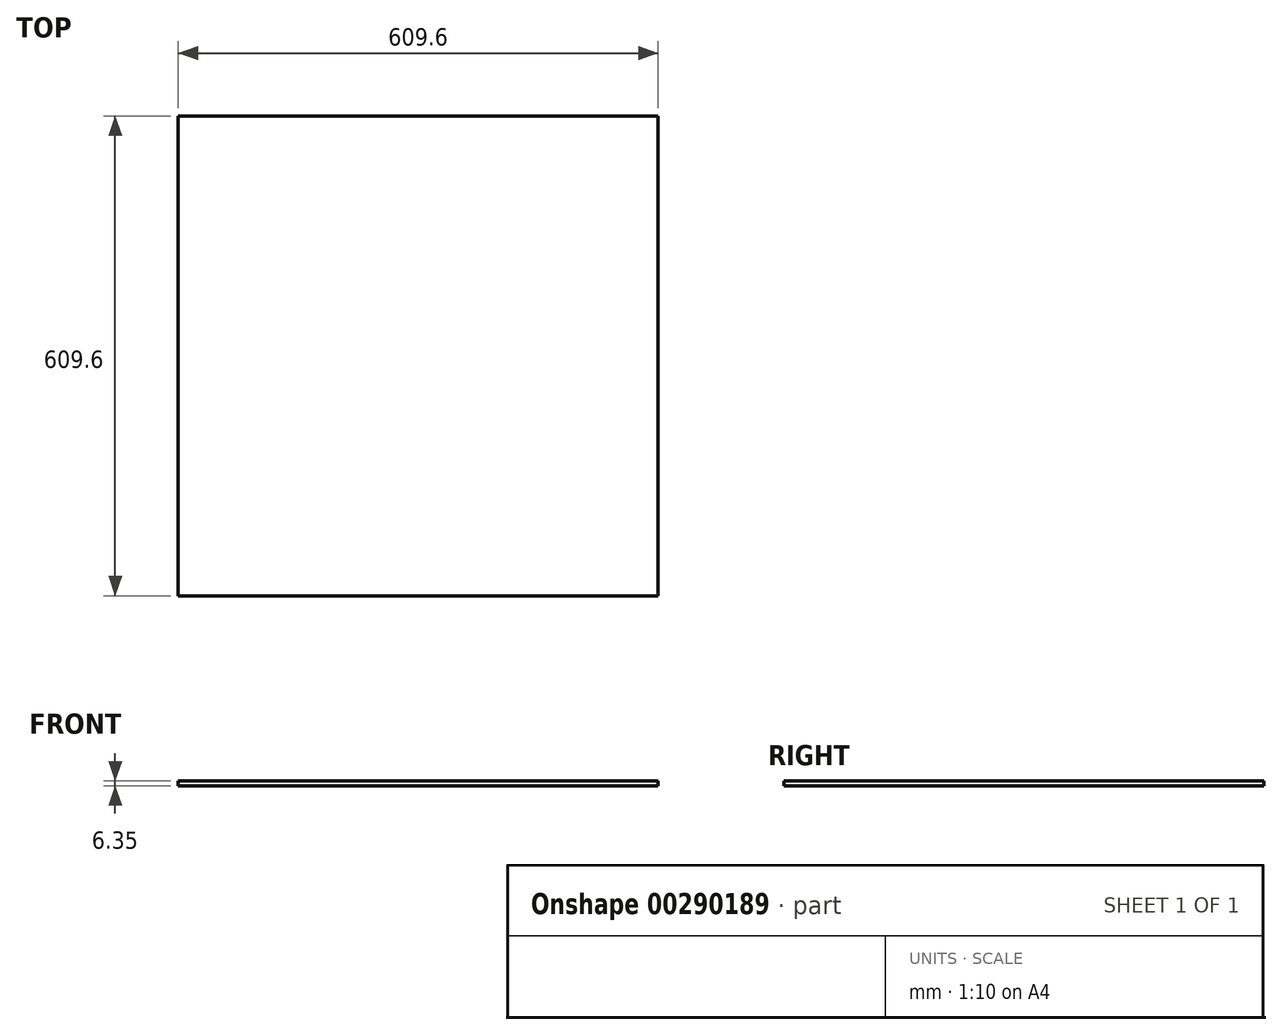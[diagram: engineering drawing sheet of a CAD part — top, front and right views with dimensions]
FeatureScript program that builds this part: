
annotation { "Feature Type Name" : "Feature", "Feature Type Description" : "" }
export const myFeature = defineFeature(function(context is Context, id is Id, definition is map)
    precondition{}
    {
        {
            var Q0;
            Q0=qCreatedBy(makeId("Top.planeOp"),FACE);
            var sketch = newSketch(context, id + "F0", { "sketchPlane" : qUnion([Q0])});
            skLineSegment(sketch, "E0.bottom", {"start": v(-304.8, 304.8) * mm, "end": v(304.8, 304.8) * mm});
            skLineSegment(sketch, "E0.top", {"start": v(-304.8, -304.8) * mm, "end": v(304.8, -304.8) * mm});
            skLineSegment(sketch, "E0.left", {"start": v(-304.8, 304.8) * mm, "end": v(-304.8, -304.8) * mm});
            skLineSegment(sketch, "E0.right", {"start": v(304.8, 304.8) * mm, "end": v(304.8, -304.8) * mm});
            skLineSegment(sketch, "E1", {"start": v(-304.8, 304.8) * mm, "end": v(304.8, -304.8) * mm, "construction": true});
            skSolve(sketch);
        }
        {
            var Q0;
            Q0 = qSketchRegion(id + "F0", true);
            extrude(context, id + "F1", {"entities" : qUnion([Q0]), "depth" : 6.35 * mm});
        }
    });
